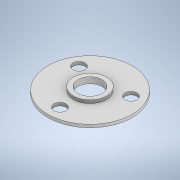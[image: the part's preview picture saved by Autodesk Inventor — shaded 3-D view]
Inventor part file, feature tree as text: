
AUTODESK INVENTOR PART (.ipt)
format: ipt  version: 2022.2 (Build 262287030, 287C)  size: 130,048 bytes
history: native  units: in
note: dims shown in document units (in); Inventor stores cm internally (conversion verified against a paired STEP export)
features: extrude x2, sketch x2, projected_geometry x1
ambient origin geometry x8: Origin, YZ Plane, XZ Plane, XY Plane, X Axis, Y Axis, Z Axis, Center Point
bodies: Solid1 (feature_tree)
feature tree (5):
  extrude  "Extrusion1"  Depth=1.0in
  extrude  "Extrusion2"  Depth=0.25in
  sketch  "Sketch1"  dims[d0=7.0in d1=1.0in]
  sketch  "Sketch3"  dims[d2=2.5in d3=2.75in d4=2.0in d5=1.1811in d7=360.0deg d9=0.25in d10=0.0in d11=2.75in d12=0.25in d13=0.0in d14=2.0in]
  projected_geometry  "Projected Loop1"
